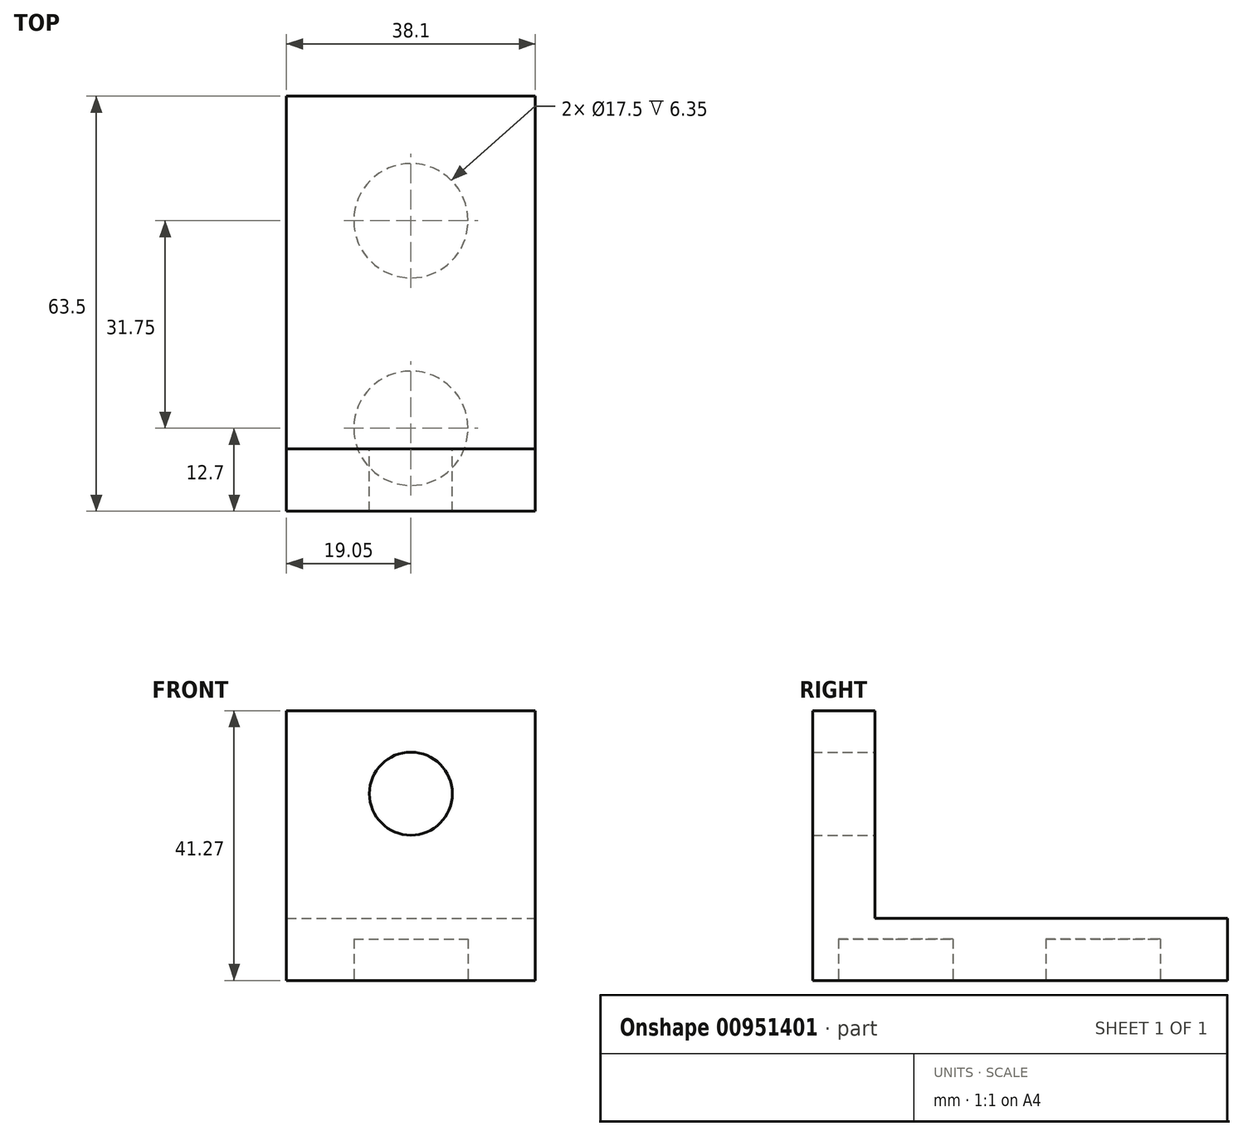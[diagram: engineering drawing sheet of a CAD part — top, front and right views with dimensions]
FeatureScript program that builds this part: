
annotation { "Feature Type Name" : "Feature", "Feature Type Description" : "" }
export const myFeature = defineFeature(function(context is Context, id is Id, definition is map)
    precondition{}
    {
        {
            var Q0;
            Q0=qCreatedBy(makeId("Top.planeOp"),FACE);
            var sketch = newSketch(context, id + "F0", { "sketchPlane" : qUnion([Q0])});
            skLineSegment(sketch, "E0.bottom", {"start": v(0, 0) * mm, "end": v(38.1, 0) * mm});
            skLineSegment(sketch, "E0.top", {"start": v(0, 63.5) * mm, "end": v(38.1, 63.5) * mm});
            skLineSegment(sketch, "E0.left", {"start": v(0, 0) * mm, "end": v(0, 63.5) * mm});
            skLineSegment(sketch, "E0.right", {"start": v(38.1, 0) * mm, "end": v(38.1, 63.5) * mm});
            skSolve(sketch);
        }
        {
            var Q0;
            Q0=makeQuery(id+"F0.imprint","IMPRINT",FACE,{"disambiguationData":[TD([[makeQuery(id+"F0.imprint","IMPRINT",EDGE,{"derivedFrom":sQuery(id+"F0.wireOp",EDGE,"E0.bottom")}),1.0]])]});
            extrude(context, id + "F1", {"entities" : qUnion([Q0]), "depth" : 9.52 * mm, "offsetDistance" : 25.4 * mm});
        }
        {
            var Q0;
            Q0=makeQuery(id+"F1.opExtrude","CAP_FACE",FACE,{"disambiguationData":[OSD([sQuery(id+"F0.wireOp",EDGE,"E0.bottom"),sQuery(id+"F0.wireOp",EDGE,"E0.top"),sQuery(id+"F0.wireOp",EDGE,"E0.left"),sQuery(id+"F0.wireOp",EDGE,"E0.right")])],"isStart":false});
            var sketch = newSketch(context, id + "F2", { "sketchPlane" : qUnion([Q0])});
            skLineSegment(sketch, "E1.bottom", {"start": v(0, 0) * mm, "end": v(38.1, 0) * mm});
            skLineSegment(sketch, "E1.top", {"start": v(0, 9.53) * mm, "end": v(38.1, 9.53) * mm});
            skLineSegment(sketch, "E1.left", {"start": v(0, 0) * mm, "end": v(0, 9.53) * mm});
            skLineSegment(sketch, "E1.right", {"start": v(38.1, 0) * mm, "end": v(38.1, 9.53) * mm});
            skSolve(sketch);
        }
        {
            var Q0;
            Q0=makeQuery(id+"F2.imprint","IMPRINT",FACE,{"disambiguationData":[TD([[makeQuery(id+"F2.imprint","IMPRINT",EDGE,{"derivedFrom":sQuery(id+"F2.wireOp",EDGE,"E1.bottom")}),1.0]])]});
            extrude(context, id + "F3", {"entities" : qUnion([Q0]), "operationType" : NewBodyOperationType.ADD, "depth" : 31.75 * mm, "offsetDistance" : 25.4 * mm});
        }
        {
            var Q0;
            Q0=makeQuery(id+"F1.opExtrude","CAP_FACE",FACE,{"disambiguationData":[OSD([sQuery(id+"F0.wireOp",EDGE,"E0.bottom"),sQuery(id+"F0.wireOp",EDGE,"E0.top"),sQuery(id+"F0.wireOp",EDGE,"E0.left"),sQuery(id+"F0.wireOp",EDGE,"E0.right")])],"isStart":true});
            var sketch = newSketch(context, id + "F4", { "sketchPlane" : qUnion([Q0])});
            skCircle(sketch, "E2", {"center": v(19.05, -44.45) * mm, "radius": 8.75 * mm});
            skCircle(sketch, "E3", {"center": v(19.05, -12.7) * mm, "radius": 8.75 * mm});
            skSolve(sketch);
        }
        {
            var Q0;
            Q0=makeQuery(id+"F4.imprint","IMPRINT",FACE,{"disambiguationData":[TD([[makeQuery(id+"F4.imprint","IMPRINT",EDGE,{"derivedFrom":sQuery(id+"F4.wireOp",EDGE,"E2")}),1.0]])]});
            extrude(context, id + "F5", {"entities" : qUnion([Q0]), "operationType" : NewBodyOperationType.REMOVE, "oppositeDirection" : true, "depth" : 6.35 * mm, "offsetDistance" : 25.4 * mm});
        }
        {
            var Q0;
            Q0=makeQuery(id+"F3.opExtrude","SWEPT_FACE",FACE,{"disambiguationData":[OSD([sQuery(id+"F2.wireOp",EDGE,"E1.top")])]});
            var sketch = newSketch(context, id + "F6", { "sketchPlane" : qUnion([Q0])});
            skCircle(sketch, "E4", {"center": v(-19.05, 28.57) * mm, "radius": 6.35 * mm});
            skSolve(sketch);
        }
        {
            var Q0;
            Q0 = qSketchRegion(id + "F6", true);
            extrude(context, id + "F7", {"entities" : qUnion([Q0]), "operationType" : NewBodyOperationType.REMOVE, "oppositeDirection" : true, "depth" : 25.4 * mm, "offsetDistance" : 25.4 * mm});
        }
        {
            var Q0;
            Q0 = qSketchRegion(id + "F4", true);
            extrude(context, id + "F8", {"entities" : qUnion([Q0]), "operationType" : NewBodyOperationType.REMOVE, "oppositeDirection" : true, "depth" : 6.35 * mm, "offsetDistance" : 25.4 * mm});
        }
    });
